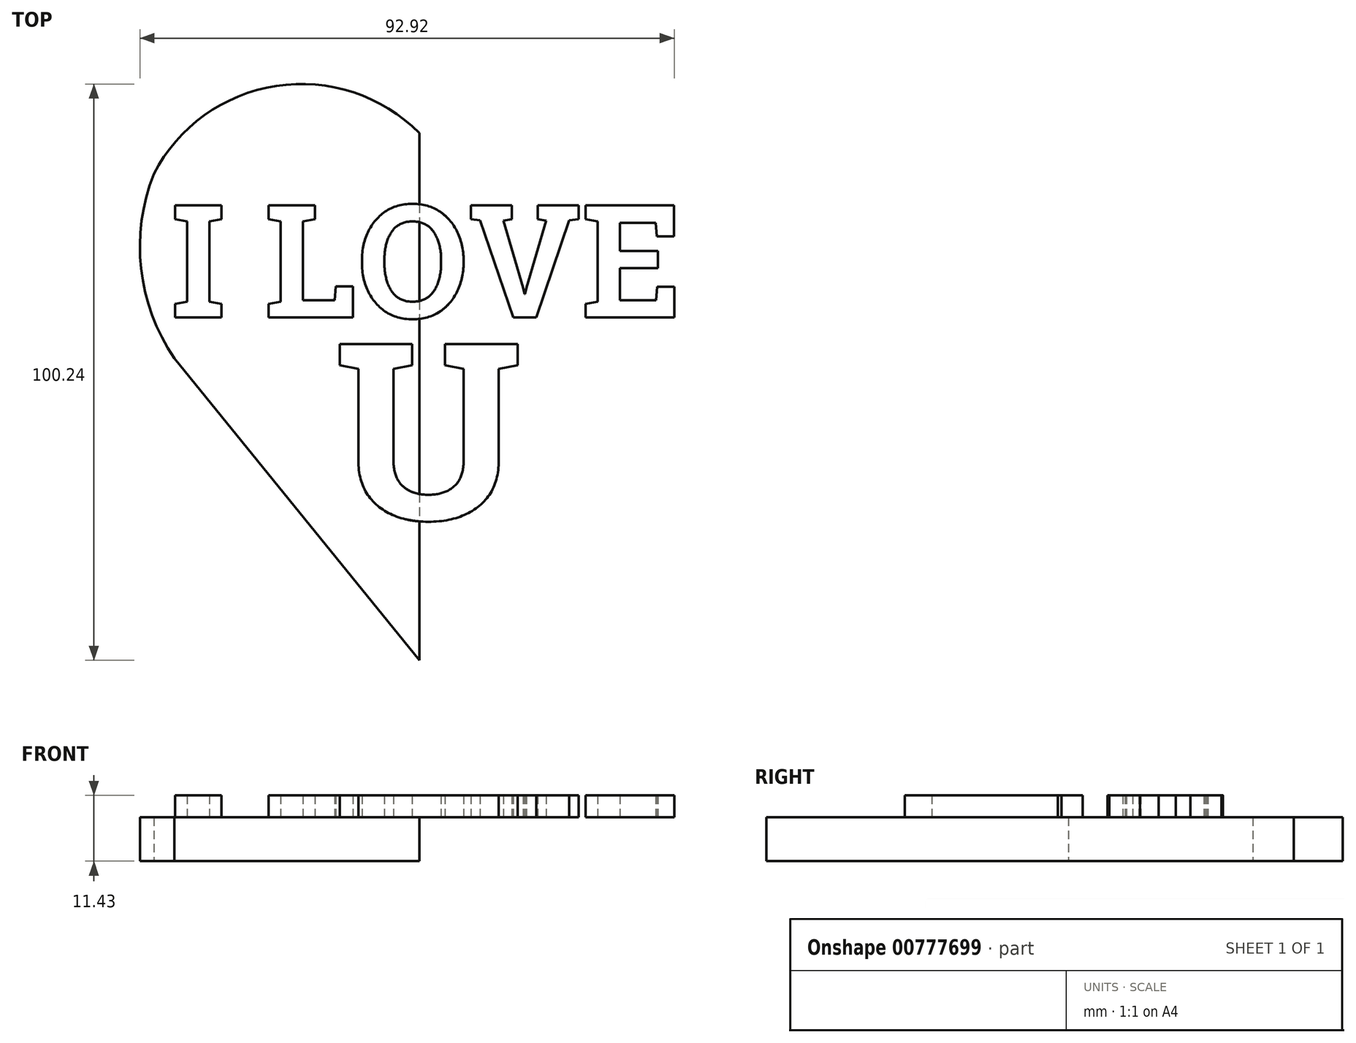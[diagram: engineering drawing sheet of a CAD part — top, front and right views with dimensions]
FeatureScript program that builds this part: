
annotation { "Feature Type Name" : "Feature", "Feature Type Description" : "" }
export const myFeature = defineFeature(function(context is Context, id is Id, definition is map)
    precondition{}
    {
        {
            var Q0;
            Q0=qCreatedBy(makeId("Top.planeOp"),FACE);
            var sketch = newSketch(context, id + "F0", { "sketchPlane" : qUnion([Q0])});
            skLineSegment(sketch, "E0", {"start": v(0, 68.57) * mm, "end": v(0, -65.6) * mm});
            skArc(sketch, "E1", {"start": v(0, 30.58) * mm, "mid": v(-24.9, 38.75) * mm, "end": v(-46.16, 23.45) * mm});
            skArc(sketch, "E2.MirrorCS", {"start": v(0, 30.58) * mm, "mid": v(24.9, 38.75) * mm, "end": v(46.16, 23.45) * mm});
            skArc(sketch, "E3", {"start": v(-46.16, 23.45) * mm, "mid": v(-48.38, 6.98) * mm, "end": v(-42.6, -8.6) * mm});
            skArc(sketch, "E4.MirrorCS", {"start": v(46.16, 23.45) * mm, "mid": v(48.38, 6.98) * mm, "end": v(42.6, -8.6) * mm});
            skLineSegment(sketch, "E5", {"start": v(-42.6, -8.6) * mm, "end": v(0, -61.15) * mm});
            skLineSegment(sketch, "E6.MirrorCS", {"start": v(42.6, -8.6) * mm, "end": v(0, -61.15) * mm});
            skSolve(sketch);
        }
        {
            var Q0;
            {var subQ0=sQuery(id+"F0.wireOp",EDGE,"E1");Q0=makeQuery(id+"F0.imprint","IMPRINT",FACE,{"disambiguationData":[TD([[makeQuery(id+"F0.imprint","IMPRINT",EDGE,{"derivedFrom":subQ0}),1.0]])]});}
            var Q1;
            {var subQ0=sQuery(id+"F0.wireOp",EDGE,"E2.MirrorCS");Q1=makeQuery(id+"F0.imprint","IMPRINT",FACE,{"disambiguationData":[TD([[makeQuery(id+"F0.imprint","IMPRINT",EDGE,{"derivedFrom":subQ0}),-1.0]])]});}
            extrude(context, id + "F1", {"entities" : qUnion([Q0, Q1]), "depth" : 7.62 * mm, "offsetDistance" : 25.4 * mm});
        }
        {
            var Q0;
            Q0=makeQuery(id+"F1.opExtrude","CAP_FACE",FACE,{"disambiguationData":[OSD([sQuery(id+"F0.wireOp",EDGE,"E1"),sQuery(id+"F0.wireOp",EDGE,"E2.MirrorCS"),sQuery(id+"F0.wireOp",EDGE,"E3"),sQuery(id+"F0.wireOp",EDGE,"E4.MirrorCS"),sQuery(id+"F0.wireOp",EDGE,"E5"),sQuery(id+"F0.wireOp",EDGE,"E6.MirrorCS")])],"isStart":false});
            var sketch = newSketch(context, id + "F2", { "sketchPlane" : qUnion([Q0])});
            skText(sketch, "E7", { "text": "I LOVE", "fontName": "RobotoSlab-Bold.ttf"});
            skText(sketch, "E8", { "text": "U", "fontName": "RobotoSlab-Bold.ttf"});
            const initialGuessF2  = {"E7": [-0.04321, -0.00153, 1, 0, 0.01974], "E8": [-0.01466, -0.0366, 1, 0, 0.03085]};
            skSetInitialGuess(sketch, initialGuessF2);
            skSolve(sketch);
        }
        {
            var Q0;
            Q0 = qSketchRegion(id + "F2", true);
            extrude(context, id + "F3", {"entities" : qUnion([Q0]), "operationType" : NewBodyOperationType.ADD, "depth" : 3.8 * mm, "offsetDistance" : 25.4 * mm});
        }
    });
